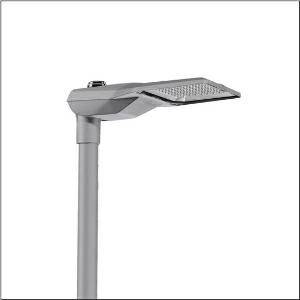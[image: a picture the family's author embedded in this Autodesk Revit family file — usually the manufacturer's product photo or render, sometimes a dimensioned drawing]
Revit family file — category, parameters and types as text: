
# Revit family: streetlight_sl_21_midi___p1_0a_5xe7a37n08lb_cb5e
name_source: partatom
category: Lighting Fixtures
units: mm (PartAtom-declared; Revit-internal decimal feet)

## family parameters
Cut with Voids When Loaded = No
Host = Face
Light Source = No
Part Type = Normal
Room Calculation Point = No
Round Connector Dimension = Use Diameter
Shared = No

## types (1)
- --- (1 x LED, 14340 lm, 98.3 W, 3000K)
    Apparent Load = 98 VA
    CIE Flux Codes = 21 50 90 100 100
    Color Rendering = 70
    Color Temperature = 3000K
    Default Elevation = 1800 mm
    Description = Streetlight SL 21 midi, mast luminaire, primary light control with lens, of PMMA, primary optical cover: cover, of toughened safety glass, transparent, light distribution: P1.0a, light emission: direct distribution, primary light characteristic: asymmetric, installation type: side-entry, LED, 3G 2.5mm², High Power LED, rated luminous flux: 14.340lm, luminous efficacy: 146lm/W, light colour: 730, colour temperature: 3000K, control: overheat protection, presetting dimming linear, constant luminous flux control, time-dependent luminous flux control, flexible luminous flux parameterisation, mains connection: 220..240V, AC, 50/60Hz, connection cable pre-assembled, cable length: 10,5m, wiring characteristics: H05VV-F, start of lifetime: 98W, end of service life: 101W, reduction: 45W, luminaire housing, of diecast aluminium (EN AC-44300), powder-coated, Siteco® metallic grey (DB 702S), corrosivity category C5 mid according to DIN EN ISO 12944, multi-level sealing system, sealing non-destructively replaceable, inclination adjustable: 0°, 5°, 10°, 15°, length: 644mm, width: 335mm, height: 110mm, spigot size: 42mm (side-entry), protection rating (complete): IP66, insulation class (complete): insulation class I (protective earthing), certification: CE, ENEC, ENEC+, VDE, impact resistance: IK09, permissible operating ambient temperature for outdoor applications: -40..+50°C, standard-compliant lighting for roads and squares, packaging unit: 1 piece

Light Distribution: P1.0a
    Height = 111 mm
    Lamp = 1 x LED
    Lamp Light Flux = 14340 lm
    Lamp Power = 98.3 W
    Lamp count = 1
    Length = 644 mm
    Luminous efficacy = 146 lm/W
    Manufacturer = Siteco
    ModVariant = No
    Model = 5XE7A37N08LB
    Number of Poles = 1
    OnlyDefault = Yes
    Power Factor = 1
    Product Name = Streetlight SL 21 midi | P1.0a
    Product group = mast luminaire | pylon top
    ProductGroupID = 6100
    Protection Class = Protection class I
    Protection Degree = IP 66
    RLX_Detail_Level = 1
    RLX_Emergency_Light_Flux = 0 lm
    RLX_Emergency_Type = 0
    RLX_Emergency_Type_DB = No
    RlxData = <blob elided: 101441 chars, md5=b0f4ec57>
    Socket = socket
    Standby Power = 0 W
    System Light Flux = 14340 lm
    System Power = 98 W
    Type Comments = factory setting: luminous flux: 100 % | dim-lin: 254 | 1020 mA
    Type Image = l_1294377.jpg
    URL = http://relux.com
    VarID = @adj_083937
    Voltage = 0 V
    Weight = 0.00 kg
    Width = 336 mm

## geometry (parser evidence)
native form markers: Blend x4, Sweep x10
no freeform markers — native parametric forms only
